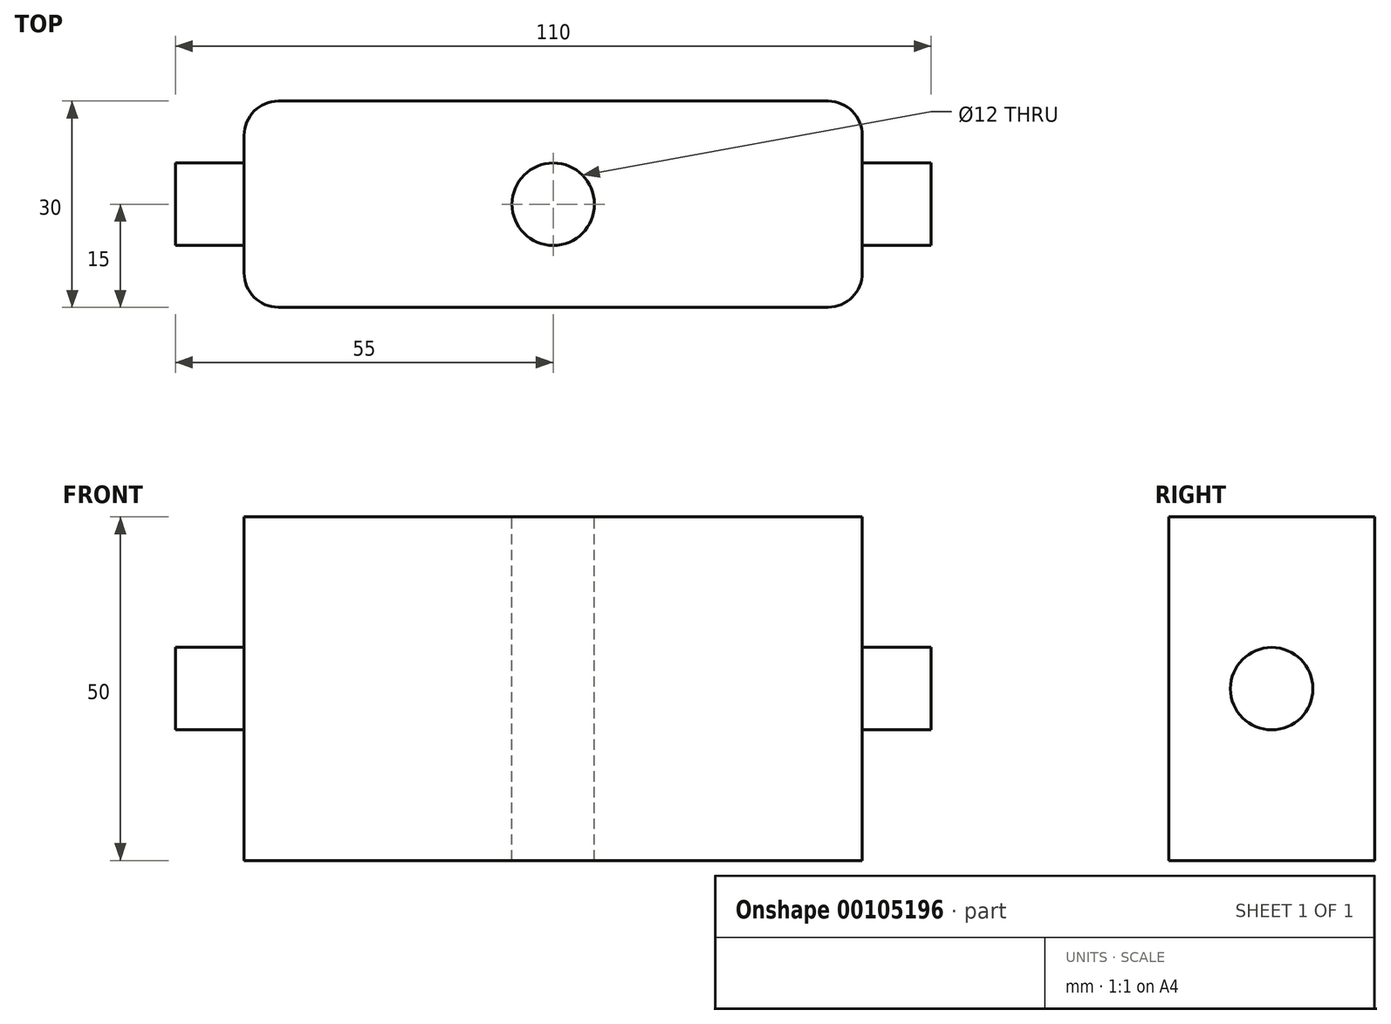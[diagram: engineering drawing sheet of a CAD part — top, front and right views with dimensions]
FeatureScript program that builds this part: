
annotation { "Feature Type Name" : "Feature", "Feature Type Description" : "" }
export const myFeature = defineFeature(function(context is Context, id is Id, definition is map)
    precondition{}
    {
        {
            var Q0;
            Q0=qCreatedBy(makeId("Top.planeOp"),FACE);
            var sketch = newSketch(context, id + "F0", { "sketchPlane" : qUnion([Q0])});
            skLineSegment(sketch, "E0.bottom", {"start": v(40, 15) * mm, "end": v(-40, 15) * mm});
            skLineSegment(sketch, "E0.top", {"start": v(40, -15) * mm, "end": v(-40, -15) * mm});
            skLineSegment(sketch, "E0.left", {"start": v(45, 10) * mm, "end": v(45, -10) * mm});
            skLineSegment(sketch, "E0.right", {"start": v(-45, 10) * mm, "end": v(-45, -10) * mm});
            skPoint(sketch, "E0.middle", {"position": v(0, 0) * mm});
            skPoint(sketch, "E1.visualSharp", {"position": v(-45, 15) * mm});
            skArc(sketch, "E1.filletArc", {"start": v(-40, 15) * mm, "mid": v(-43.54, 13.54) * mm, "end": v(-45, 10) * mm});
            skPoint(sketch, "E2.visualSharp", {"position": v(45, 15) * mm});
            skArc(sketch, "E2.filletArc", {"start": v(45, 10) * mm, "mid": v(43.54, 13.54) * mm, "end": v(40, 15) * mm});
            skPoint(sketch, "E3.visualSharp", {"position": v(45, -15) * mm});
            skArc(sketch, "E3.filletArc", {"start": v(40, -15) * mm, "mid": v(43.54, -13.54) * mm, "end": v(45, -10) * mm});
            skPoint(sketch, "E4.visualSharp", {"position": v(-45, -15) * mm});
            skArc(sketch, "E4.filletArc", {"start": v(-45, -10) * mm, "mid": v(-43.54, -13.54) * mm, "end": v(-40, -15) * mm});
            skSolve(sketch);
        }
        {
            var Q0;
            Q0=makeQuery(id+"F0.imprint","IMPRINT",FACE,{"disambiguationData":[TD([[makeQuery(id+"F0.imprint","IMPRINT",EDGE,{"derivedFrom":sQuery(id+"F0.wireOp",EDGE,"E0.bottom")}),1.0]])]});
            extrude(context, id + "F1", {"entities" : qUnion([Q0]), "depth" : 50 * mm});
        }
        {
            var Q0;
            Q0=makeQuery(id+"F1.opExtrude","SWEPT_FACE",FACE,{"disambiguationData":[OSD([sQuery(id+"F0.wireOp",EDGE,"E0.right")])]});
            var sketch = newSketch(context, id + "F2", { "sketchPlane" : qUnion([Q0])});
            skCircle(sketch, "E5", {"center": v(0, 25) * mm, "radius": 6 * mm});
            skPoint(sketch, "E5.centerSnap0", {"position": v(10, 25) * mm});
            skSolve(sketch);
        }
        {
            var Q0;
            Q0 = qSketchRegion(id + "F2", true);
            extrude(context, id + "F3", {"entities" : qUnion([Q0]), "operationType" : NewBodyOperationType.ADD, "depth" : 10 * mm});
        }
        {
            var Q0;
            Q0 = qSketchRegion(id + "F2", true);
            extrude(context, id + "F4", {"entities" : qUnion([Q0]), "operationType" : NewBodyOperationType.ADD, "oppositeDirection" : true, "depth" : 100 * mm});
        }
        {
            var Q0;
            Q0=makeQuery(id+"F1.opExtrude","CAP_FACE",FACE,{"disambiguationData":[OSD([sQuery(id+"F0.wireOp",EDGE,"E0.bottom"),sQuery(id+"F0.wireOp",EDGE,"E0.top"),sQuery(id+"F0.wireOp",EDGE,"E0.left"),sQuery(id+"F0.wireOp",EDGE,"E0.right"),sQuery(id+"F0.wireOp",EDGE,"E1.filletArc"),sQuery(id+"F0.wireOp",EDGE,"E2.filletArc"),sQuery(id+"F0.wireOp",EDGE,"E3.filletArc"),sQuery(id+"F0.wireOp",EDGE,"E4.filletArc")])],"isStart":false});
            var sketch = newSketch(context, id + "F5", { "sketchPlane" : qUnion([Q0])});
            skCircle(sketch, "E6", {"center": v(0, 0) * mm, "radius": 6 * mm});
            skSolve(sketch);
        }
        {
            var Q0;
            Q0 = qSketchRegion(id + "F5", true);
            extrude(context, id + "F6", {"entities" : qUnion([Q0]), "operationType" : NewBodyOperationType.REMOVE, "endBound" : BoundingType.THROUGH_ALL, "oppositeDirection" : true, "depth" : 25 * mm});
        }
    });
